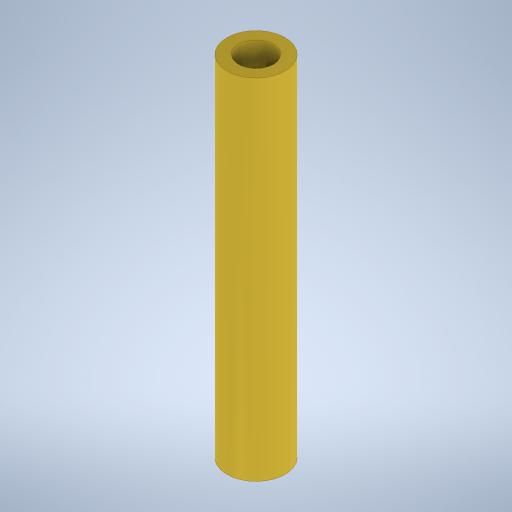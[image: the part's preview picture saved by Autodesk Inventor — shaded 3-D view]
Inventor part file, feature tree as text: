
AUTODESK INVENTOR PART (.ipt)
format: ipt  version: 2023 (Build 270158000, 158)  size: 228,864 bytes
history: native  units: in
note: dims shown in document units (in); Inventor stores cm internally (conversion verified against a paired STEP export)
features: extrude x1, sketch x1
ambient origin geometry x8: Origin, YZ Plane, XZ Plane, XY Plane, X Axis, Y Axis, Z Axis, Center Point
bodies: Solid1 (feature_tree)
feature tree (2):
  extrude  "Extrusion1"  Depth=1.1811in
  sketch  "Sketch1"  dims[d0=0.1969in d1=0.1181in d2=1.1811in d3=0.0in]
